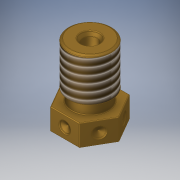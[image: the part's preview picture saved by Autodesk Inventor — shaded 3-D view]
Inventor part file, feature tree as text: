
AUTODESK INVENTOR PART (.ipt)
format: ipt  version: 2019 (Build 230136000, 136)  size: 392,704 bytes
history: native  units: mm
features: sketch x6, extrude x5, chamfer x3, other x2, pattern_circular x1, fillet x1
ambient origin geometry x8: Origin, YZ Plane, XZ Plane, XY Plane, X Axis, Y Axis, Z Axis, Center Point
bodies: Solide1 (feature_tree)
feature tree (18):
  other  "Révolution1"
  extrude  "Extrusion1"  Depth=3.0mm
  extrude  "Extrusion2"  Depth=6.0mm
  chamfer  "Chanfrein1"  Distance=0.5mm
  pattern_circular  "Réseau circulaire1"  [2 undecoded]
  extrude  "Extrusion3"  Depth=1.0mm
  extrude  "Extrusion4"  Depth=3.0mm
  extrude  "Extrusion5"  Depth=12.5mm
  chamfer  "Chanfrein2"  Angle=60.0deg  [1 undecoded]
  other  "Filetage1"
  chamfer  "Chanfrein3"  Distance=0.5mm
  fillet  "Congé1"  [1 undecoded]
  sketch  "Esquisse1"
  sketch  "Esquisse3"
  sketch  "Esquisse4"
  sketch  "Esquisse5"
  sketch  "Esquisse6"
  sketch  "Esquisse7"
note: 4 required parameter values undecoded (feature->parameter linkage not recoverable at this tier; creation-order binding heuristic only, values carry confidence <= 0.55)
